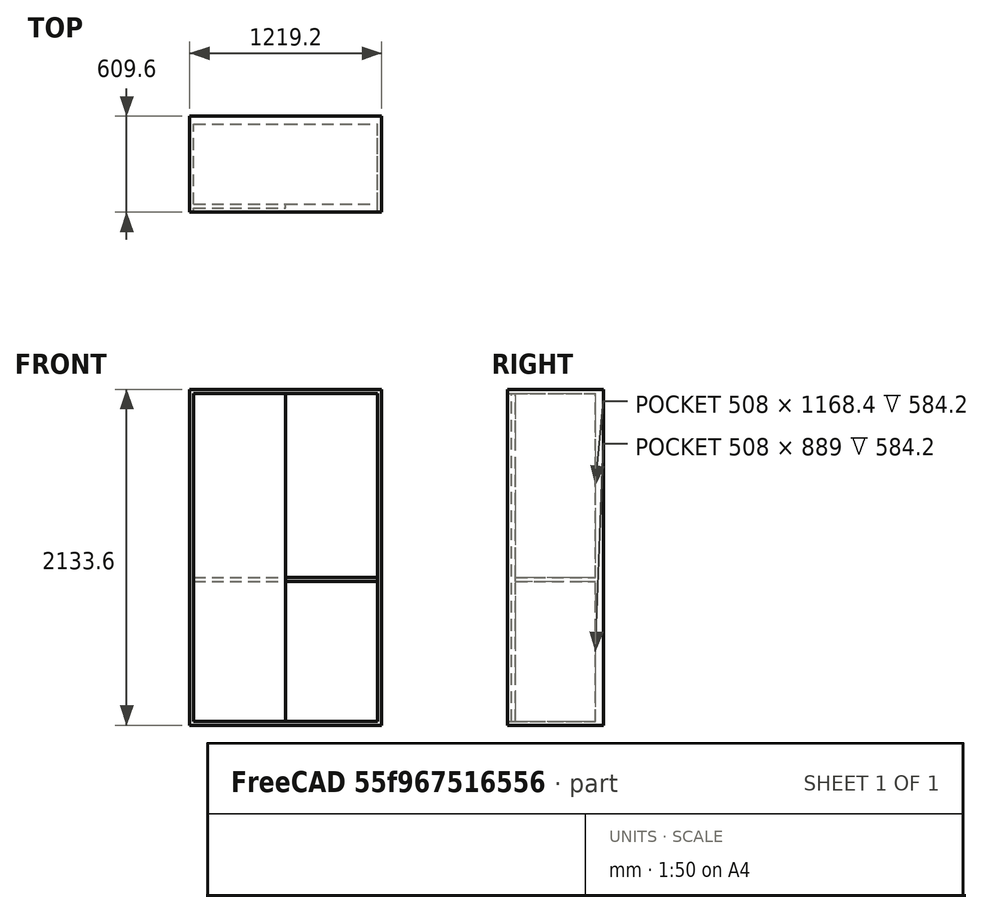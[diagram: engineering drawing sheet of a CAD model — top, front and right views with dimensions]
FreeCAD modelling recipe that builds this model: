
FCSTD DOCUMENT  (FreeCAD 0.17R7668 (Git))
Label: Generic - Kitchenette cabinet
License: All rights reserved
LicenseURL: http://en.wikipedia.org/wiki/All_rights_reserved
objects: Part::Box×3, Part::Cut×2, Part::Feature×1, Part::MultiFuse×1
note: 7 computed .brp shape members not serialized (recipe doc carries the construction recipe); baked Part::Feature solids carry a one-line shape summary decoded from their .brp

FEATURE [Part::Feature] Generic___Cabinet
  shape: bbox 1219 x 609.6 x 2134 mm, 11 faces (baked)
FEATURE [Part::Box] Box  label="Cube"
  AttacherType = Attacher::AttachEngine3D
  Height = 2082.8
  Length = 584.2
  Placement = pos=(609.6,0,25.4) rot=(0,0,1;0rad)
  Width = 558.8
FEATURE [Part::Cut] Cut
  Base = -> Generic___Cabinet
  Tool = -> Box
FEATURE [Part::Box] Box001  label="Cube001"
  AttacherType = Attacher::AttachEngine3D
  Height = 2082.8
  Length = 584.2
  Placement = pos=(25.4,50.8,25.4) rot=(0,0,1;0rad)
  Width = 508
FEATURE [Part::Cut] Cut001
  Base = -> Cut
  Tool = -> Box001
FEATURE [Part::Box] Box002  label="Cube002"
  AttacherType = Attacher::AttachEngine3D
  Height = 25.4
  Length = 1168.4
  Placement = pos=(25.4,50.8,914.4) rot=(0,0,1;0rad)
  Width = 508
FEATURE [Part::MultiFuse] Fusion
  Shapes = -> [Cut001,Box002]
